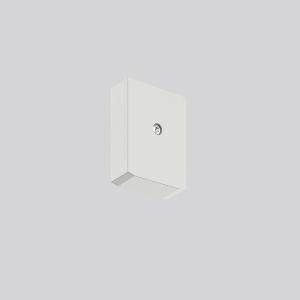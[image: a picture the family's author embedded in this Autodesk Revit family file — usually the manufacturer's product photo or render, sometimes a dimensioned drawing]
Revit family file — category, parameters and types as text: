
# Revit family: linedo_endkappe_b_f_982700_009_3cd6
name_source: partatom
category: Lighting Fixtures
units: mm (PartAtom-declared; Revit-internal decimal feet)

## family parameters
Cut with Voids When Loaded = No
Host = Face
Light Source = No
Part Type = Normal
Room Calculation Point = No
Round Connector Dimension = Use Diameter
Shared = No

## types (1)
- LINEDO_Endkappe_B_F
    Apparent Load = 0 VA
    Default Elevation = 1800 mm
    Description = End cap low profile for LINEDO plug. Plastic end cap to cover the LINEDO plug system at the end of the line. Fastening by TX20 screw. Installation accessories included.
Colour: grey
Length: 23 mm
Width: 58 mm
Height: 76 mm
Weight: 31 g
    Height = 76 mm
    Lamp = 0 x
    Length = 23 mm
    Luminous efficacy = 0 lm/W
    Manufacturer = RZB
    ModVariant = No
    Model = 982700.009
    Mounting Place = Ceiling
    Mounting Type = Surface mounted, Pendant
    Number of Poles = 1
    OnlyDefault = Yes
    Power Factor = 1
    Product Name = LINEDO_Endkappe_B_F
    Product group = Surface mounted continuous line luminaire system
    ProductGroupID = 310
    Protection Class = Protection class
    Protection Degree = Degree of protection
    RLX_Detail_Level = 1
    RLX_Emergency_Light_Flux = 0 lm
    RLX_Emergency_Type = 0
    RLX_Emergency_Type_DB = No
    RlxData = <blob elided: 8445 chars, md5=6ae8f0b0>
    Standby Power = 0 W
    System Light Flux = 0 lm
    System Power = 0 W
    Type Comments = Product without accessories
    Type Image = 982700.009.jpg
    URL = http://relux.com
    VarID = ---
    Voltage = 0 V
    Weight = 0.00 kg
    Width = 58 mm

## geometry (parser evidence)
native form markers: Sweep x9
no freeform markers — native parametric forms only
